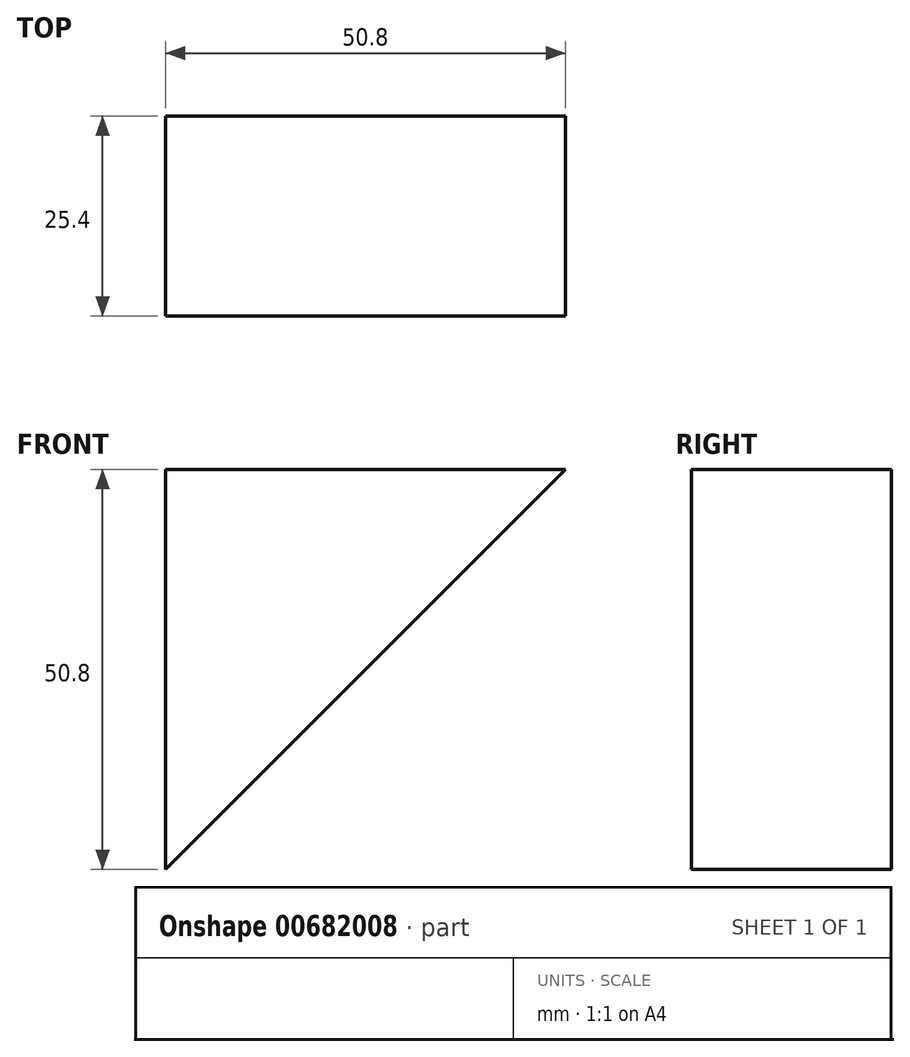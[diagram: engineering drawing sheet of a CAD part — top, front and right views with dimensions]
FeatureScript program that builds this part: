
annotation { "Feature Type Name" : "Feature", "Feature Type Description" : "" }
export const myFeature = defineFeature(function(context is Context, id is Id, definition is map)
    precondition{}
    {
        {
            var Q0;
            Q0=qCreatedBy(makeId("Front.planeOp"),FACE);
            var sketch = newSketch(context, id + "F0", { "sketchPlane" : qUnion([Q0])});
            skLineSegment(sketch, "E0", {"start": v(0, 0) * mm, "end": v(0, 50.8) * mm});
            skLineSegment(sketch, "E1", {"start": v(0, 50.8) * mm, "end": v(50.8, 50.8) * mm});
            skLineSegment(sketch, "E2", {"start": v(50.8, 50.8) * mm, "end": v(0, 0) * mm});
            skSolve(sketch);
        }
        {
            var Q0;
            Q0 = qSketchRegion(id + "F0", true);
            extrude(context, id + "F1", {"entities" : qUnion([Q0]), "depth" : 25.4 * mm, "offsetDistance" : 25.4 * mm});
        }
    });
